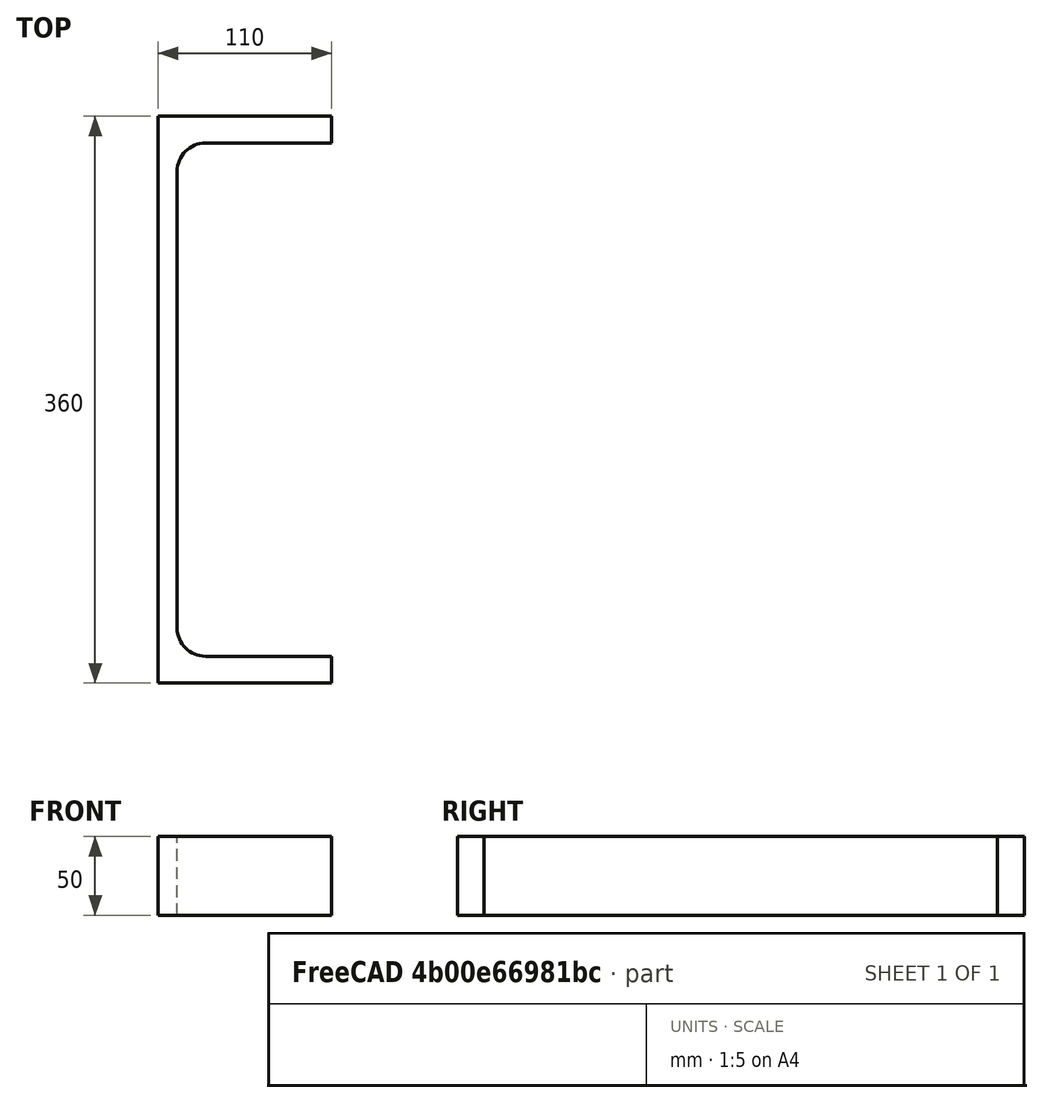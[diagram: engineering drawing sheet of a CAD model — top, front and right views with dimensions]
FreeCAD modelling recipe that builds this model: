
FCSTD DOCUMENT  (FreeCAD 0.20R29410 (Git))
Label: UPE-Profile 360 DIN1026-2 S235JR
License: All rights reserved
LicenseURL: http://en.wikipedia.org/wiki/All_rights_reserved
objects: Sketcher::SketchObject×1, Part::Extrusion×1
note: 2 computed .brp shape members not serialized (recipe doc carries the construction recipe); baked Part::Feature solids carry a one-line shape summary decoded from their .brp

FEATURE [Sketcher::SketchObject] Sketch
  FullyConstrained = true
  MapMode = 5
  sketch-geometry (10):
    g0: LineSegment StartX=12 StartY=-145 StartZ=0 EndX=12 EndY=145 EndZ=0
    g1: LineSegment StartX=30 StartY=163 StartZ=0 EndX=110 EndY=163 EndZ=0
    g2: LineSegment StartX=110 StartY=163 StartZ=0 EndX=110 EndY=180 EndZ=0
    g3: LineSegment StartX=110 StartY=-180 StartZ=0 EndX=110 EndY=-163 EndZ=0
    g4: LineSegment StartX=110 StartY=-163 StartZ=0 EndX=30 EndY=-163 EndZ=0
    g5: ArcOfCircle CenterX=30 CenterY=145 CenterZ=0 NormalX=0 NormalY=0 NormalZ=1 AngleXU=0 Radius=18 StartAngle=1.5708 EndAngle=3.14159
    g6: ArcOfCircle CenterX=30 CenterY=-145 CenterZ=0 NormalX=0 NormalY=0 NormalZ=1 AngleXU=0 Radius=18 StartAngle=3.14159 EndAngle=4.71239
    g7: LineSegment StartX=110 StartY=-180 StartZ=0 EndX=0 EndY=-180 EndZ=0
    g8: LineSegment StartX=0 StartY=-180 StartZ=0 EndX=0 EndY=180 EndZ=0
    g9: LineSegment StartX=0 StartY=180 StartZ=0 EndX=110 EndY=180 EndZ=0
  constraints (27):
    c: Vertical(g0)
    c: Coincident(g2,g1)
    c: Vertical(g2)
    c: Vertical(g3)
    c: Coincident(g4,g3)
    c: Horizontal(g4)
    c: Tangent(g1,g5) = 1.5708
    c: Tangent(g0,g5) = 1.5708
    c: Tangent(g0,g6) = 1.5708
    c: Tangent(g4,g6) = 1.5708
    c: Symmetric(g2,g3,g-1)
    c: DistanceY(g2) = 17
    c: Radius(g5) = 18
    c: Coincident(g3,g7)
    c: PointOnObject(g7,g-2)
    c: Horizontal(g7)
    c: Coincident(g7,g8)
    c: PointOnObject(g8,g-2)
    c: Coincident(g8,g9)
    c: Coincident(g9,g2)
    c: Horizontal(g9)
    c: Distance(g-1,g0) = 12
    c: DistanceX(g9,g9) = 110
    c: Horizontal(g1)
    c: Equal(g3,g2)
    c: Equal(g5,g6)
    c: DistanceY(g3,g2) = 360
FEATURE [Part::Extrusion] Extrude  label="UPE-Profile 360 DIN1026-2 S235JR"
  Base = -> Sketch
  Dir = (0,0,50)
  DirMode = 0
  FaceMakerClass = Part::FaceMakerExtrusion
  LengthFwd = 0
  LengthRev = 0
  Solid = true
  Symmetric = false
